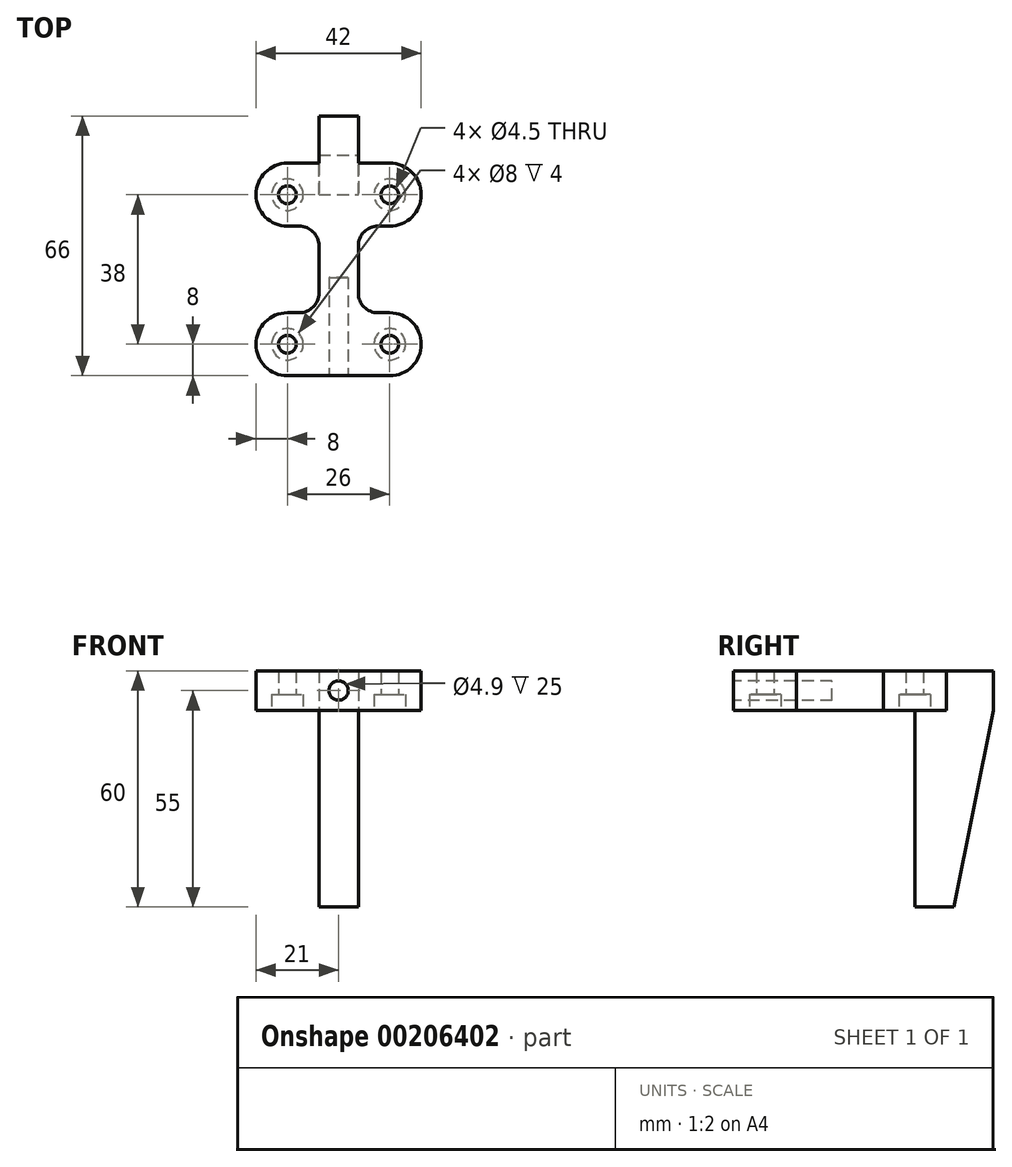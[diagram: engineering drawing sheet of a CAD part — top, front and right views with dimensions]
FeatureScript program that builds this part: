
annotation { "Feature Type Name" : "Feature", "Feature Type Description" : "" }
export const myFeature = defineFeature(function(context is Context, id is Id, definition is map)
    precondition{}
    {
        {
            var Q0;
            Q0=qCreatedBy(makeId("Top.planeOp"),FACE);
            var sketch = newSketch(context, id + "F0", { "sketchPlane" : qUnion([Q0])});
            skCircle(sketch, "E0", {"center": v(-13, 0) * mm, "radius": 2.25 * mm});
            skCircle(sketch, "E1.MirrorC", {"center": v(13, 0) * mm, "radius": 2.25 * mm});
            skCircle(sketch, "E2", {"center": v(-13, -38) * mm, "radius": 2.25 * mm});
            skCircle(sketch, "E3.MirrorC", {"center": v(13, -38) * mm, "radius": 2.25 * mm});
            skLineSegment(sketch, "E4", {"start": v(0, 8) * mm, "end": v(-13, 8) * mm});
            skArc(sketch, "E5", {"start": v(-13, 8) * mm, "mid": v(-21, 0) * mm, "end": v(-13, -8) * mm});
            skArc(sketch, "E6", {"start": v(-13, -46) * mm, "mid": v(-21, -38) * mm, "end": v(-13, -30) * mm});
            skLineSegment(sketch, "E7", {"start": v(-13, -46) * mm, "end": v(0, -46) * mm});
            skLineSegment(sketch, "E8.MirrorCS", {"start": v(13, -46) * mm, "end": v(0, -46) * mm});
            skArc(sketch, "E9.MirrorCS", {"start": v(13, -46) * mm, "mid": v(21, -38) * mm, "end": v(13, -30) * mm});
            skArc(sketch, "E10.MirrorCS", {"start": v(13, 8) * mm, "mid": v(21, 0) * mm, "end": v(13, -8) * mm});
            skLineSegment(sketch, "E11.MirrorCS", {"start": v(0, 8) * mm, "end": v(13, 8) * mm});
            skLineSegment(sketch, "E12", {"start": v(-13, -8) * mm, "end": v(-10, -8) * mm});
            skLineSegment(sketch, "E13", {"start": v(-5, -13) * mm, "end": v(-5, -25) * mm});
            skLineSegment(sketch, "E14", {"start": v(-13, -30) * mm, "end": v(-10, -30) * mm});
            skPoint(sketch, "E15.visualSharp", {"position": v(-5, -8) * mm});
            skArc(sketch, "E15.filletArc", {"start": v(-5, -13) * mm, "mid": v(-6.46, -9.46) * mm, "end": v(-10, -8) * mm});
            skPoint(sketch, "E16.visualSharp", {"position": v(-5, -30) * mm});
            skArc(sketch, "E16.filletArc", {"start": v(-10, -30) * mm, "mid": v(-6.46, -28.54) * mm, "end": v(-5, -25) * mm});
            skLineSegment(sketch, "E17.MirrorCS", {"start": v(13, -8) * mm, "end": v(10, -8) * mm});
            skArc(sketch, "E18.MirrorCS", {"start": v(5, -13) * mm, "mid": v(6.46, -9.46) * mm, "end": v(10, -8) * mm});
            skLineSegment(sketch, "E19.MirrorCS", {"start": v(5, -13) * mm, "end": v(5, -25) * mm});
            skArc(sketch, "E20.MirrorCS", {"start": v(10, -30) * mm, "mid": v(6.46, -28.54) * mm, "end": v(5, -25) * mm});
            skLineSegment(sketch, "E21.MirrorCS", {"start": v(13, -30) * mm, "end": v(10, -30) * mm});
            skSolve(sketch);
        }
        {
            var Q0;
            Q0 = qSketchRegion(id + "F0", true);
            extrude(context, id + "F1", {"entities" : qUnion([Q0]), "depth" : 10 * mm});
        }
        {
            var Q0;
            Q0=makeQuery(id+"F1.opExtrude","SWEPT_FACE",FACE,{"disambiguationData":[OSD([sQuery(id+"F0.wireOp",EDGE,"E19.MirrorCS")])]});
            var sketch = newSketch(context, id + "F2", { "sketchPlane" : qUnion([Q0])});
            skLineSegment(sketch, "E22", {"start": v(0, 0) * mm, "end": v(0, -50) * mm});
            skLineSegment(sketch, "E23", {"start": v(0, -50) * mm, "end": v(10, -50) * mm});
            skLineSegment(sketch, "E24", {"start": v(10, -50) * mm, "end": v(20, 0) * mm});
            skLineSegment(sketch, "E25", {"start": v(20, 0) * mm, "end": v(0, 0) * mm});
            skLineSegment(sketch, "E26", {"start": v(20, 0) * mm, "end": v(20, 10) * mm});
            skLineSegment(sketch, "E27", {"start": v(20, 10) * mm, "end": v(8, 10) * mm});
            skLineSegment(sketch, "E28", {"start": v(8, 10) * mm, "end": v(8, 0) * mm});
            skSolve(sketch);
        }
        {
            var Q0;
            Q0 = qSketchRegion(id + "F2", true);
            extrude(context, id + "F3", {"entities" : qUnion([Q0]), "operationType" : NewBodyOperationType.ADD, "oppositeDirection" : true, "depth" : 10 * mm});
        }
        {
            var Q0;
            Q0=makeQuery(id+"F1.opExtrude","SWEPT_FACE",FACE,{"disambiguationData":[OSD([sQuery(id+"F0.wireOp",EDGE,"E7"),sQuery(id+"F0.wireOp",EDGE,"E8.MirrorCS")])]});
            var sketch = newSketch(context, id + "F4", { "sketchPlane" : qUnion([Q0])});
            skCircle(sketch, "E29", {"center": v(0, 5) * mm, "radius": 2.45 * mm});
            skSolve(sketch);
        }
        {
            var Q0;
            Q0 = qSketchRegion(id + "F4", true);
            extrude(context, id + "F5", {"entities" : qUnion([Q0]), "operationType" : NewBodyOperationType.REMOVE, "oppositeDirection" : true, "depth" : 25 * mm});
        }
        {
            var Q0;
            Q0=makeQuery(id+"F1.opExtrude","CAP_FACE",FACE,{"disambiguationData":[OSD([sQuery(id+"F0.wireOp",EDGE,"E0"),sQuery(id+"F0.wireOp",EDGE,"E1.MirrorC"),sQuery(id+"F0.wireOp",EDGE,"E2"),sQuery(id+"F0.wireOp",EDGE,"E3.MirrorC"),sQuery(id+"F0.wireOp",EDGE,"E4"),sQuery(id+"F0.wireOp",EDGE,"E5"),sQuery(id+"F0.wireOp",EDGE,"E6"),sQuery(id+"F0.wireOp",EDGE,"E7"),sQuery(id+"F0.wireOp",EDGE,"E8.MirrorCS"),sQuery(id+"F0.wireOp",EDGE,"E9.MirrorCS"),sQuery(id+"F0.wireOp",EDGE,"E10.MirrorCS"),sQuery(id+"F0.wireOp",EDGE,"E11.MirrorCS"),sQuery(id+"F0.wireOp",EDGE,"E12"),sQuery(id+"F0.wireOp",EDGE,"E13"),sQuery(id+"F0.wireOp",EDGE,"E14"),sQuery(id+"F0.wireOp",EDGE,"E15.filletArc"),sQuery(id+"F0.wireOp",EDGE,"E16.filletArc"),sQuery(id+"F0.wireOp",EDGE,"E17.MirrorCS"),sQuery(id+"F0.wireOp",EDGE,"E18.MirrorCS"),sQuery(id+"F0.wireOp",EDGE,"E19.MirrorCS"),sQuery(id+"F0.wireOp",EDGE,"E20.MirrorCS"),sQuery(id+"F0.wireOp",EDGE,"E21.MirrorCS")])],"isStart":true});
            var sketch = newSketch(context, id + "F6", { "sketchPlane" : qUnion([Q0])});
            skCircle(sketch, "E30", {"center": v(13, 0) * mm, "radius": 4 * mm});
            skCircle(sketch, "E31", {"center": v(-13, 0) * mm, "radius": 4 * mm});
            skCircle(sketch, "E32", {"center": v(-13, 38) * mm, "radius": 4 * mm});
            skCircle(sketch, "E33", {"center": v(13, 38) * mm, "radius": 4 * mm});
            skSolve(sketch);
        }
        {
            var Q0;
            Q0 = qSketchRegion(id + "F6", true);
            extrude(context, id + "F7", {"entities" : qUnion([Q0]), "operationType" : NewBodyOperationType.REMOVE, "oppositeDirection" : true, "depth" : 4 * mm});
        }
    });
